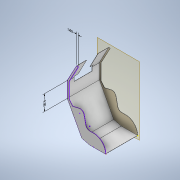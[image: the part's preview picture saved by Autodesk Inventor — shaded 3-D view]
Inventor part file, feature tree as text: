
AUTODESK INVENTOR PART (.ipt)
format: ipt  version: 2021 (Build 250183000, 183)  size: 225,280 bytes
history: native  units: in
note: dims shown in document units (in); Inventor stores cm internally (conversion verified against a paired STEP export)
features: sketch x6, extrude x4, other x3, plane x1
ambient origin geometry x8: Origin, YZ Plane, XZ Plane, XY Plane, X Axis, Y Axis, Z Axis, Center Point
bodies: Solid1 (feature_tree)
feature tree (14):
  other  "Annotations"
  sketch  "Sketch1"  dims[d63=0.125in d64=0.5in]
  extrude  "Extrusion1"  Depth=0.125in
  extrude  "Extrusion2"  Depth=0.125in
  plane  "Work Plane3"
  sketch  "Sketch5"  dims[d68=0.125in d69=18.5in d70=0.0in]
  sketch  "Sketch6"  dims[d71=0.125in d72=0.0in d73=-18.5in]
  extrude  "Extrusion3"  Depth=18.5in TaperAngle=0.0deg
  extrude  "Extrusion4"  [1 undecoded]
  sketch  "Sketch4"  dims[d65=0.125in d66=0.125in]
  sketch  "Sketch7"  dims[d74=0.125in d75=0.0in]
  sketch  "Sketch8"  dims[d77=9.0in d78=23.5in d80=5.25in d81=5.25in d82=20.0in d83=10.5in d84=1.0in d85=1.875in d86=1.875in d87=36.0in d88=0.0in d90=0.125in d92=0.125in d93=0.125in d96=0.0in d97=0.0in d57=1.0004in d76=9.0in d24=0.5in d25=0.0344in d26=0.5in d27=0.0344in d89=0.5in d91=0.5in]
  other  "Linear Dimension 1"
  other  "Linear Dimension 2"
note: 1 required parameter value undecoded (feature->parameter linkage not recoverable at this tier; creation-order binding heuristic only, values carry confidence <= 0.55)
